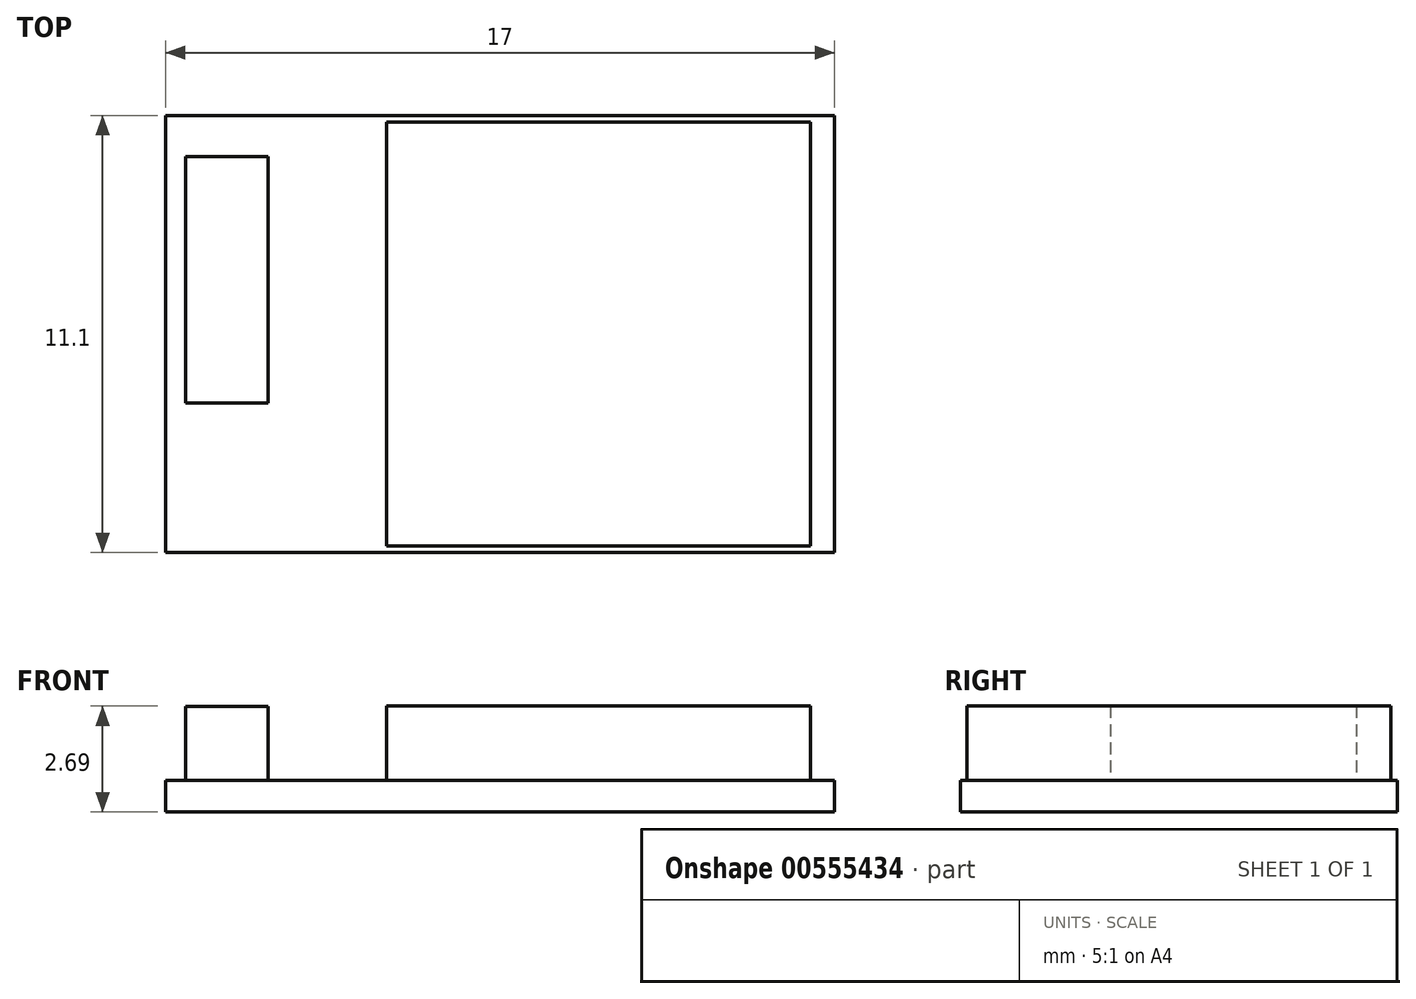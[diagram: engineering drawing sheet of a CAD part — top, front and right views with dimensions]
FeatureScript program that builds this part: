
annotation { "Feature Type Name" : "Feature", "Feature Type Description" : "" }
export const myFeature = defineFeature(function(context is Context, id is Id, definition is map)
    precondition{}
    {
        {
            var Q0;
            Q0=qCreatedBy(makeId("Top.planeOp"),FACE);
            var sketch = newSketch(context, id + "F0", { "sketchPlane" : qUnion([Q0])});
            skLineSegment(sketch, "E0.bottom", {"start": v(-8.5, 5.55) * mm, "end": v(8.5, 5.55) * mm});
            skLineSegment(sketch, "E0.top", {"start": v(-8.5, -5.55) * mm, "end": v(8.5, -5.55) * mm});
            skLineSegment(sketch, "E0.left", {"start": v(-8.5, 5.55) * mm, "end": v(-8.5, -5.55) * mm});
            skLineSegment(sketch, "E0.right", {"start": v(8.5, 5.55) * mm, "end": v(8.5, -5.55) * mm});
            skPoint(sketch, "E0.middle", {"position": v(0, 0) * mm});
            skSolve(sketch);
        }
        {
            var Q0;
            Q0 = qSketchRegion(id + "F0", true);
            extrude(context, id + "F1", {"entities" : qUnion([Q0]), "depth" : 0.8 * mm, "offsetDistance" : 25.4 * mm});
        }
        {
            var Q0;
            Q0=makeQuery(id+"F1.opExtrude","CAP_FACE",FACE,{"disambiguationData":[OSD([sQuery(id+"F0.wireOp",EDGE,"E0.bottom"),sQuery(id+"F0.wireOp",EDGE,"E0.top"),sQuery(id+"F0.wireOp",EDGE,"E0.left"),sQuery(id+"F0.wireOp",EDGE,"E0.right")])],"isStart":false});
            var sketch = newSketch(context, id + "F2", { "sketchPlane" : qUnion([Q0])});
            skLineSegment(sketch, "E1.bottom", {"start": v(-2.88, 5.38) * mm, "end": v(7.89, 5.38) * mm});
            skLineSegment(sketch, "E1.top", {"start": v(-2.88, -5.38) * mm, "end": v(7.89, -5.38) * mm});
            skLineSegment(sketch, "E1.left", {"start": v(-2.88, 5.38) * mm, "end": v(-2.88, -5.38) * mm});
            skLineSegment(sketch, "E1.right", {"start": v(7.89, 5.38) * mm, "end": v(7.89, -5.38) * mm});
            skPoint(sketch, "E1.middle", {"position": v(2.5, 0) * mm});
            skSolve(sketch);
        }
        {
            var Q0;
            Q0 = qSketchRegion(id + "F2", true);
            extrude(context, id + "F3", {"entities" : qUnion([Q0]), "operationType" : NewBodyOperationType.ADD, "depth" : 1.9 * mm, "offsetDistance" : 25.4 * mm});
        }
        {
            var Q0;
            Q0=makeQuery(id+"F1.opExtrude","CAP_FACE",FACE,{"disambiguationData":[OSD([sQuery(id+"F0.wireOp",EDGE,"E0.bottom"),sQuery(id+"F0.wireOp",EDGE,"E0.top"),sQuery(id+"F0.wireOp",EDGE,"E0.left"),sQuery(id+"F0.wireOp",EDGE,"E0.right")])],"isStart":false});
            var sketch = newSketch(context, id + "F4", { "sketchPlane" : qUnion([Q0])});
            skLineSegment(sketch, "E2.bottom", {"start": v(-8, 4.5) * mm, "end": v(-5.9, 4.5) * mm});
            skLineSegment(sketch, "E2.top", {"start": v(-8, -1.75) * mm, "end": v(-5.9, -1.75) * mm});
            skLineSegment(sketch, "E2.left", {"start": v(-8, 4.5) * mm, "end": v(-8, -1.75) * mm});
            skLineSegment(sketch, "E2.right", {"start": v(-5.9, 4.5) * mm, "end": v(-5.9, -1.75) * mm});
            skSolve(sketch);
        }
        {
            var Q0;
            Q0 = qSketchRegion(id + "F4", true);
            extrude(context, id + "F5", {"entities" : qUnion([Q0]), "operationType" : NewBodyOperationType.ADD, "depth" : 2.69 * mm - 0.8 * mm, "offsetDistance" : 25.4 * mm});
        }
    });
